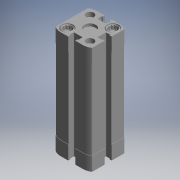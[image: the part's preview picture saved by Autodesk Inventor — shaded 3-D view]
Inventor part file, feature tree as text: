
AUTODESK INVENTOR PART (.ipt)
format: ipt  version: 2017.3 (Build 213256000, 256)  size: 694,272 bytes
history: native  units: mm (DEFAULTED — no unit token found)
features: other x63, sketch x30, revolve x13, hole x11, thread x8, extrude x6
ambient origin geometry x8: Origin, YZ Plane, XZ Plane, XY Plane, X Axis, Y Axis, Z Axis, Center Point
bodies: Solid1 (feature_tree)
feature tree (131):
  extrude  "Extrusion1"  Depth=63.0mm TaperAngle=0.0deg
  extrude  "Extrusion2"  TaperAngle=360.0deg  [1 undecoded]
  hole  "Hole1"  [1 undecoded]
  hole  "Hole2"  [1 undecoded]
  revolve  "Revolution1"  Angle=360.0deg
  hole  "Hole3"  [1 undecoded]
  hole  "Hole4"  [1 undecoded]
  revolve  "Revolution2"  Angle=360.0deg
  thread  "Thread1"  [1 undecoded]
  hole  "Hole5"  [1 undecoded]
  revolve  "Revolution3"  Angle=360.0deg
  thread  "Thread2"  [1 undecoded]
  hole  "Hole6"  [1 undecoded]
  hole  "Hole7"  [1 undecoded]
  revolve  "Revolution4"  [1 undecoded]
  thread  "Thread3"  [1 undecoded]
  revolve  "Revolution5"  [1 undecoded]
  thread  "Thread4"  [1 undecoded]
  revolve  "Revolution6"  [1 undecoded]
  thread  "Thread5"  [1 undecoded]
  revolve  "Revolution7"  [1 undecoded]
  hole  "Hole8"  [1 undecoded]
  revolve  "Revolution8"  [1 undecoded]
  thread  "Thread6"  [1 undecoded]
  revolve  "Revolution9"  [1 undecoded]
  hole  "Hole9"  [1 undecoded]
  revolve  "Revolution10"  [1 undecoded]
  thread  "Thread7"  [1 undecoded]
  revolve  "Revolution11"  [1 undecoded]
  hole  "Hole10"  [1 undecoded]
  revolve  "Revolution12"  [1 undecoded]
  thread  "Thread8"  [1 undecoded]
  revolve  "Revolution13"  [1 undecoded]
  hole  "Hole11"  [1 undecoded]
  extrude  "Extrusion3"  [1 undecoded]
  extrude  "Extrusion4"  [1 undecoded]
  extrude  "Extrusion5"  [1 undecoded]
  extrude  "Extrusion6"  [1 undecoded]
  other  "CYLINDER_XY"
  other  "CYLINDER_YZ"
  other  "CYLINDER_ZX"
  other  "CYLINDER_X"
  other  "CYLINDER_Y"
  other  "CYLINDER_Z"
  other  "CYLINDER_Center"
  other  "FDT_FRONT_XY"
  other  "FDT_FRONT_YZ"
  other  "FDT_FRONT_ZX"
  other  "FDT_FRONT_X"
  other  "FDT_FRONT_Y"
  other  "FDT_FRONT_Z"
  other  "FDT_FRONT_Center"
  other  "FDT_QSFRONT_XY"
  other  "FDT_QSFRONT_YZ"
  other  "FDT_QSFRONT_ZX"
  other  "FDT_QSFRONT_X"
  other  "FDT_QSFRONT_Y"
  other  "FDT_QSFRONT_Z"
  other  "FDT_QSFRONT_Center"
  other  "FDT_QSREAR_XY"
  other  "FDT_QSREAR_YZ"
  other  "FDT_QSREAR_ZX"
  other  "FDT_QSREAR_X"
  other  "FDT_QSREAR_Y"
  other  "FDT_QSREAR_Z"
  other  "FDT_QSREAR_Center"
  other  "FDT_REAR_XY"
  other  "FDT_REAR_YZ"
  other  "FDT_REAR_ZX"
  other  "FDT_REAR_X"
  other  "FDT_REAR_Y"
  other  "FDT_REAR_Z"
  other  "FDT_REAR_Center"
  other  "FDT_SLOT3_1_XY"
  other  "FDT_SLOT3_1_YZ"
  other  "FDT_SLOT3_1_ZX"
  other  "FDT_SLOT3_1_X"
  other  "FDT_SLOT3_1_Y"
  other  "FDT_SLOT3_1_Z"
  other  "FDT_SLOT3_1_Center"
  other  "FDT_SLOT5_1_XY"
  other  "FDT_SLOT5_1_YZ"
  other  "FDT_SLOT5_1_ZX"
  other  "FDT_SLOT5_1_X"
  other  "FDT_SLOT5_1_Y"
  other  "FDT_SLOT5_1_Z"
  other  "FDT_SLOT5_1_Center"
  other  "FDT_SLOT7_1_XY"
  other  "FDT_SLOT7_1_YZ"
  other  "FDT_SLOT7_1_ZX"
  other  "FDT_SLOT7_1_X"
  other  "FDT_SLOT7_1_Y"
  other  "FDT_SLOT7_1_Z"
  other  "FDT_SLOT7_1_Center"
  other  "TO_DUMMY_XY"
  other  "TO_DUMMY_YZ"
  other  "TO_DUMMY_ZX"
  other  "TO_DUMMY_X"
  other  "TO_DUMMY_Y"
  other  "TO_DUMMY_Z"
  other  "TO_DUMMY_Center"
  sketch  "Skizze_1"  dims[d0=85.0mm d1=0.0mm d2=63.0mm d3=0.0mm]
  sketch  "Sketch_111"
  sketch  "Sketch3"  dims[d4=4.134mm d5=5.933mm d6=5.0mm d7=2.0mm d8=90.0deg d9=6.7mm d10=0.0mm]
  sketch  "Sketch4"  dims[d19=9.0mm d20=6.0mm d21=4.0mm d22=2.0mm d23=90.0deg d24=2.1mm d25=0.0mm]
  sketch  "Skizze_5"  dims[d34=13.121mm d35=0.0mm]
  sketch  "Sketch6"  dims[d36=6.0mm d37=6.0mm d38=9.2mm d39=5.0mm d40=90.0deg d41=17.0mm d42=0.0mm d43=360.0deg]
  sketch  "Sketch7"  dims[d44=13.121mm d45=0.0mm]
  sketch  "Sketch_27"  dims[d118=0.0mm d119=0.0mm d120=0.0mm d121=0.0mm d122=0.0mm d123=0.0mm d124=0.0mm d125=0.0mm d126=0.0mm]
  sketch  "Sketch9"  dims[d61=13.121mm d62=0.0mm d63=360.0deg]
  sketch  "Sketch_28"
  sketch  "Sketch11"  dims[d70=4.0mm d71=6.0mm d72=4.0mm d73=2.0mm d74=90.0deg d75=57.0mm d76=0.0mm d77=360.0deg]
  sketch  "Sketch12"  dims[d78=7.121mm d79=0.0mm d80=360.0deg]
  sketch  "Sketch_29"
  sketch  "Sketch_30"
  sketch  "Skizze_12"  dims[d81=4.0mm d82=6.0mm d83=4.0mm d84=2.0mm d85=90.0deg d86=57.0mm d87=0.0mm d88=360.0deg d89=7.121mm d90=0.0mm]
  sketch  "Sketch_123"
  sketch  "Sketch17"  dims[d92=4.0mm d93=6.0mm d94=4.0mm d95=2.0mm d96=90.0deg d97=57.0mm d98=0.0mm d99=360.0deg]
  sketch  "Sketch_3"  dims[d11=4.134mm d12=5.933mm d13=5.0mm d14=2.0mm d15=90.0deg d16=9.0mm d17=0.0mm d18=360.0deg]
  sketch  "Sketch_117"
  sketch  "Sketch20"  dims[d100=7.121mm d101=0.0mm d102=360.0deg]
  sketch  "Skizze_13"  dims[d91=360.0deg]
  sketch  "Sketch_121"
  sketch  "Sketch23"  dims[d103=4.0mm d104=6.0mm d105=4.0mm d106=2.0mm d107=90.0deg d108=57.0mm d109=0.0mm d110=3.0mm d111=0.0mm d112=3.0mm d113=0.0mm]
  sketch  "Sketch_4"  dims[d26=6.0mm d27=6.0mm d28=9.2mm d29=5.0mm d30=90.0deg d31=17.0mm d32=0.0mm d33=360.0deg]
  sketch  "Sketch_118"
  sketch  "Sketch26"  dims[d114=3.0mm d115=0.0mm d116=3.0mm d117=0.0mm]
  sketch  "Sketch_8"  dims[d53=6.0mm d54=6.0mm d55=9.2mm d56=5.0mm d57=90.0deg d58=17.0mm d59=0.0mm d60=360.0deg]
  sketch  "Sketch_7"  dims[d46=6.0mm d47=6.0mm d48=9.2mm d49=5.0mm d50=90.0deg d51=17.0mm d52=0.0mm]
  sketch  "Sketch_9"  dims[d64=13.121mm d65=0.0mm d66=360.0deg]
  sketch  "Sketch_10"  dims[d67=7.121mm d68=0.0mm d69=360.0deg]
note: 34 required parameter values undecoded (feature->parameter linkage not recoverable at this tier; creation-order binding heuristic only, values carry confidence <= 0.55)